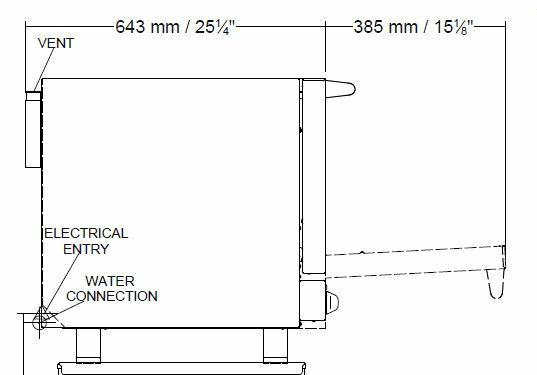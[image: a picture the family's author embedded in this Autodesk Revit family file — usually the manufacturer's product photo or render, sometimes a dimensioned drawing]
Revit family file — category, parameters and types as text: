
# Revit family: QF_MOFFAT_E27D3_NZ
name_source: partatom
category: Specialty Equipment
revit_build: Autodesk Revit 2014 (Build: 20130308_1515(x64)
units: mm (PartAtom-declared; Revit-internal decimal feet)

## types (1)
- QF_MOFFAT_E27D3_NZ
    Apparent Power = 4508 VA
    Cold Water Connection Height = 0 mm  [stored 0 ft]
    Cold Water Flow = 0 GPM
    Cold Water Maximum Pressure = 80.00 psi
    Cold Water Minimum Pressure = 20.00 psi
    Cold Water RI Height = 0 mm  [stored 0 ft]
    Cold Water Size = 1"
    Cold Water Temperature Recommended = 0 °F
    Conn Conduit = Yes
    Cycle = 50 Hz
    Depth = 762 mm  [stored 2.5 ft]
    Description = FULL SIZE DIGITAL / ELECTRIC CONVECTION OVEN ON A STAINLESS STEEL STAND
    Elec Conn Connection Height = 0 mm  [stored 0 ft]
    Elec Conn RI Height = 0 mm  [stored 0 ft]
    Electrical Remarks = 230-240V, 50Hz, 1P+N+E, 4.7kW, 19.6A
    Exhaust RI Height = 0 mm  [stored 0 ft]
    Exhaust Static Press = 0.00 in-wg
    Exhaust Vent Depth = 0 mm  [stored 0 ft]
    Exhaust Vent Diameter = 0 mm  [stored 0 ft]
    Exhaust Vent Width = 0 mm  [stored 0 ft]
    Exhaust Volume = 0 CFM
    FL Amps = 20 A
    Foodservice Equipment Identifier = Yes
    Height = 1487 mm  [stored 4.87861 ft]
    Height of Stand = 880 mm  [stored 2.88714 ft]
    Identify Quantity as Lot = Yes
    Length = 810 mm
    Manufacturer = MOFFAT
    Max Overcurrent Protection = 0 A
    Min Ckt Ampacity = 0 A
    Model = E27D3
    Number of Poles = 1
    Phase = 1
    URL = www.moffat.com.au
    URL Cutsheet = www.moffat.com.au
    Volts = 230 V
    Watts = 4700 W
    Weight in Pounds = 0

note: [stored X ft] marks values corroborated as IEEE doubles in the binary element streams (Revit-internal decimal feet)

## geometry (parser evidence)
native form markers: Blend x12, Sweep x9
no freeform markers — native parametric forms only
